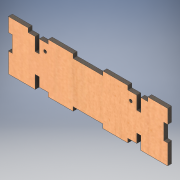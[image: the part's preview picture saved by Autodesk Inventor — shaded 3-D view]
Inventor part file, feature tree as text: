
AUTODESK INVENTOR PART (.ipt)
format: ipt  version: 2019 (Build 230136000, 136)  size: 185,856 bytes
history: native  units: mm
features: extrude x2, sketch x2, other x1
ambient origin geometry x8: Origin, YZ Plane, XZ Plane, XY Plane, X Axis, Y Axis, Z Axis, Center Point
bodies: Body1 (feature_tree)
feature tree (5):
  other  "Твердое тело1"
  extrude  "Выдавливание1"  Depth=4.0mm
  extrude  "Выдавливание2"  Depth=30.0mm
  sketch  "Эскиз1"
  sketch  "Эскиз2"
